# Revit family: 1711 Spine Lounge Suite Petit
name_source: partatom
category: Furniture
revit_build: Autodesk Revit 2017 (Build: 20171027_0315(x64)
units: mm (PartAtom-declared; Revit-internal decimal feet)

## family parameters
Always vertical = Yes
Cut with Voids When Loaded = No
OmniClass Number = 23.40.20.00
OmniClass Title = General Furniture and Specialties
Room Calculation Point = No
Shared = No
Work Plane-Based = No

## types (1)
- 1711 Spine Lounge Suite Petit
    Cushion = FF Black Leather 88
    Depth = 70 cm
    Description = Spine Lounge Suite Petit is a light lounge chair for private homes or open lounge areas. The generous use of materials is balanced by its discreet design. The accented detailing on the wooden back makes the chair as beautiful standing mid-room as it is against a wall.
    Design year = 2016
    Designer = Space Copenhagen
    Frame = FF Black Lacquered horizontal
    Height = 69 cm
    Item No. = 1711
    Legs = FF Black Lacquered vertical
    Manufacturer = Fredericia Furniture
    Model = Spine Lounge Suite Chair
    Seat Height = 41 cm
    Type Comments = Lounge Series
    URL = https://www.fredericia.com
    Variation Legs = Available in other kind of wood
    Variations = Avalible with felt gliders
    Variations Frame = Available in other kind of wood
    Variations Upholster = Available in fabric and leather
    Weight = 17,5kg
    Width = 65 cm

## geometry (parser evidence)
native form markers: Sweep x2
no freeform markers — native parametric forms only
